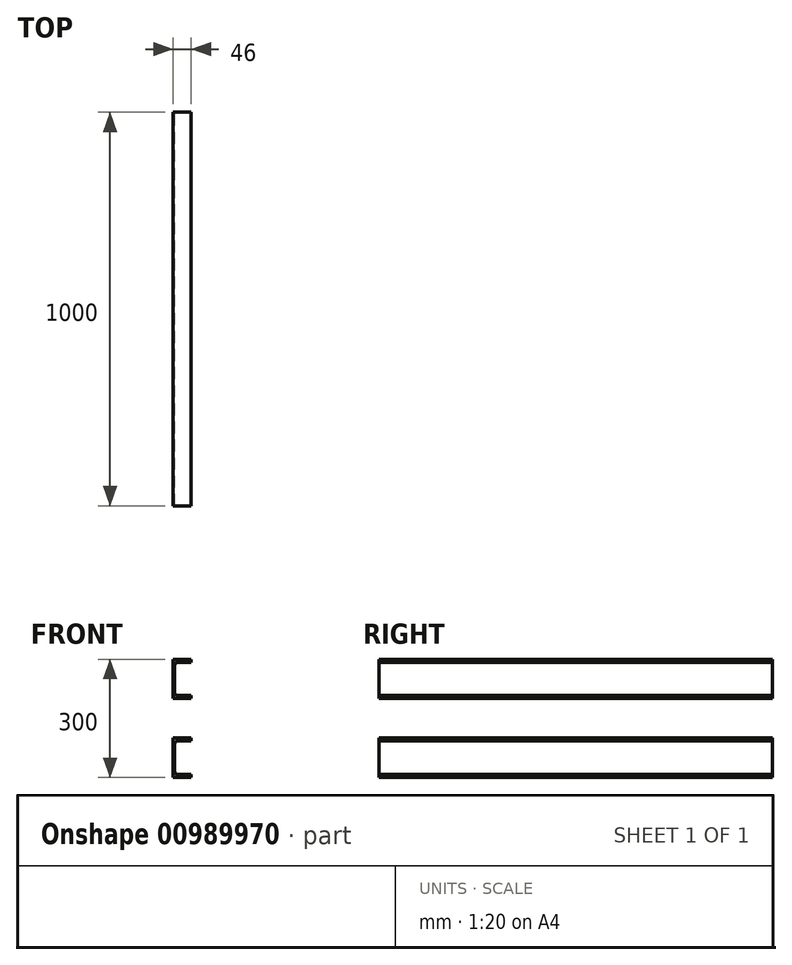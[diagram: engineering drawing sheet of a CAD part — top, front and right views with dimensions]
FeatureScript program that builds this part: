
annotation { "Feature Type Name" : "Feature", "Feature Type Description" : "" }
export const myFeature = defineFeature(function(context is Context, id is Id, definition is map)
    precondition{}
    {
        {
            var Q0;
            Q0=qCreatedBy(makeId("Front.planeOp"),FACE);
            var sketch = newSketch(context, id + "F0", { "sketchPlane" : qUnion([Q0])});
            skLineSegment(sketch, "E0", {"start": v(-3.81, -50) * mm, "end": v(-3.81, -150) * mm});
            skLineSegment(sketch, "E1", {"start": v(-3.81, -50) * mm, "end": v(42.19, -50) * mm});
            skLineSegment(sketch, "E2", {"start": v(42.19, -50) * mm, "end": v(42.19, -57.6) * mm});
            skLineSegment(sketch, "E3", {"start": v(42.19, -57.6) * mm, "end": v(7.69, -57.6) * mm});
            skLineSegment(sketch, "E4", {"start": v(0.69, -64.6) * mm, "end": v(0.69, -135.4) * mm});
            skLineSegment(sketch, "E5", {"start": v(7.69, -142.4) * mm, "end": v(42.19, -142.4) * mm});
            skLineSegment(sketch, "E6", {"start": v(42.19, -142.4) * mm, "end": v(42.19, -150) * mm});
            skLineSegment(sketch, "E7", {"start": v(42.19, -150) * mm, "end": v(-3.81, -150) * mm});
            skPoint(sketch, "E8.visualSharp", {"position": v(0.69, -57.6) * mm});
            skArc(sketch, "E8.filletArc", {"start": v(7.69, -57.6) * mm, "mid": v(2.74, -59.65) * mm, "end": v(0.69, -64.6) * mm});
            skPoint(sketch, "E9.visualSharp", {"position": v(0.69, -142.4) * mm});
            skArc(sketch, "E9.filletArc", {"start": v(0.69, -135.4) * mm, "mid": v(2.74, -140.35) * mm, "end": v(7.69, -142.4) * mm});
            skArc(sketch, "E10.MirrorCS", {"start": v(0.69, 135.4) * mm, "mid": v(2.74, 140.35) * mm, "end": v(7.69, 142.4) * mm});
            skLineSegment(sketch, "E11.MirrorCS", {"start": v(42.19, 50) * mm, "end": v(42.19, 57.6) * mm});
            skLineSegment(sketch, "E12.MirrorCS", {"start": v(42.19, 142.4) * mm, "end": v(42.19, 150) * mm});
            skArc(sketch, "E13.MirrorCS", {"start": v(7.69, 57.6) * mm, "mid": v(2.74, 59.65) * mm, "end": v(0.69, 64.6) * mm});
            skLineSegment(sketch, "E14.MirrorCS", {"start": v(-3.81, 50) * mm, "end": v(42.19, 50) * mm});
            skLineSegment(sketch, "E15.MirrorCS", {"start": v(42.19, 57.6) * mm, "end": v(7.69, 57.6) * mm});
            skLineSegment(sketch, "E16.MirrorCS", {"start": v(-3.81, 50) * mm, "end": v(-3.81, 150) * mm});
            skPoint(sketch, "E17.MirrorP", {"position": v(0.69, 57.6) * mm});
            skLineSegment(sketch, "E18.MirrorCS", {"start": v(0.69, 64.6) * mm, "end": v(0.69, 135.4) * mm});
            skLineSegment(sketch, "E19.MirrorCS", {"start": v(7.69, 142.4) * mm, "end": v(42.19, 142.4) * mm});
            skLineSegment(sketch, "E20.MirrorCS", {"start": v(42.19, 150) * mm, "end": v(-3.81, 150) * mm});
            skPoint(sketch, "E21.MirrorP", {"position": v(0.69, 142.4) * mm});
            skSolve(sketch);
        }
        {
            var Q0;
            Q0 = qSketchRegion(id + "F0", true);
            var Q1;
            Q1=makeQuery(id+"F0.imprint","IMPRINT",FACE,{"disambiguationData":[TD([[makeQuery(id+"F0.imprint","IMPRINT",EDGE,{"derivedFrom":sQuery(id+"F0.wireOp",EDGE,"E0")}),1.0]])]});
            extrude(context, id + "F1", {"entities" : qUnion([Q0, Q1]), "depth" : 1000 * mm, "offsetDistance" : 25 * mm});
        }
    });
